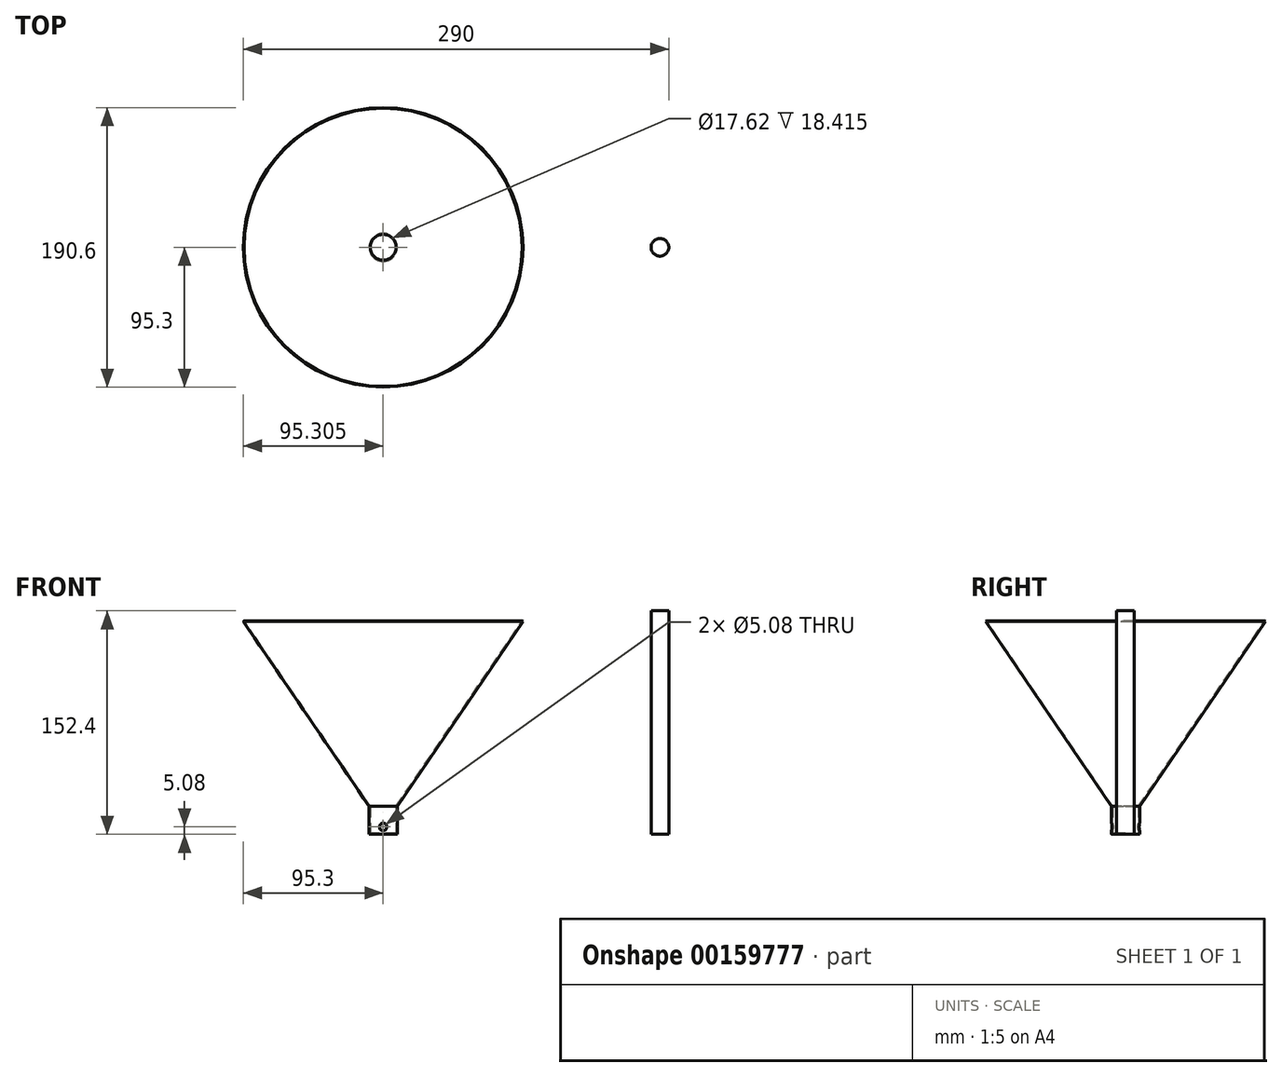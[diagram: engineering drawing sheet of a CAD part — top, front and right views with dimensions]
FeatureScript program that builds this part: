
annotation { "Feature Type Name" : "Feature", "Feature Type Description" : "" }
export const myFeature = defineFeature(function(context is Context, id is Id, definition is map)
    precondition{}
    {
        {
            var Q0;
            Q0=qCreatedBy(makeId("Top.planeOp"),FACE);
            var sketch = newSketch(context, id + "F0", { "sketchPlane" : qUnion([Q0])});
            skCircle(sketch, "E0", {"center": v(0, 0) * mm, "radius": 6.35 * mm});
            skSolve(sketch);
        }
        {
            var Q0;
            Q0=makeQuery(id+"F0.imprint","IMPRINT",FACE,{"disambiguationData":[TD([[makeQuery(id+"F0.imprint","IMPRINT",EDGE,{"derivedFrom":sQuery(id+"F0.wireOp",EDGE,"E0")}),1.0]])]});
            extrude(context, id + "F1", {"entities" : qUnion([Q0]), "depth" : 0.64 * mm});
        }
        {
            var Q0;
            Q0=makeQuery(id+"F1.opExtrude","CAP_FACE",FACE,{"disambiguationData":[OSD([sQuery(id+"F0.wireOp",EDGE,"E0")])],"isStart":false});
            var sketch = newSketch(context, id + "F2", { "sketchPlane" : qUnion([Q0])});
            skCircle(sketch, "E1", {"center": v(0, 0) * mm, "radius": 5.72 * mm});
            skSolve(sketch);
        }
        {
            var Q0;
            Q0=makeQuery(id+"F2.imprint","IMPRINT",FACE,{"disambiguationData":[TD([[makeQuery(id+"F2.imprint","IMPRINT",EDGE,{"derivedFrom":sQuery(id+"F2.wireOp",EDGE,"E1")}),-1.0]])]});
            extrude(context, id + "F3", {"entities" : qUnion([Q0]), "operationType" : NewBodyOperationType.ADD, "depth" : 12.7 * mm});
        }
        {
            var Q0;
            Q0=qCreatedBy(makeId("Front.planeOp"),FACE);
            var sketch = newSketch(context, id + "F4", { "sketchPlane" : qUnion([Q0])});
            skCircle(sketch, "E2", {"center": v(0, 3.18) * mm, "radius": 2.22 * mm});
            skSolve(sketch);
        }
        {
            var Q0;
            Q0=makeQuery(id+"F4.imprint","IMPRINT",FACE,{"disambiguationData":[TD([[makeQuery(id+"F4.imprint","IMPRINT",EDGE,{"derivedFrom":sQuery(id+"F4.wireOp",EDGE,"E2")}),1.0]])]});
            var Q1;
            Q1=sQuery(id+"F4.wireOp",EDGE,"E2");
            extrude(context, id + "F5", {"entities" : qUnion([Q0]), "operationType" : NewBodyOperationType.REMOVE, "surfaceEntities" : qUnion([Q1]), "endBound" : BoundingType.THROUGH_ALL, "oppositeDirection" : true, "depth" : 25.4 * mm, "hasSecondDirection" : true, "secondDirectionBound" : SecondDirectionBoundingType.THROUGH_ALL, "secondDirectionOppositeDirection" : false, "secondDirectionDepth" : 25.4 * mm});
        }
        {
            var Q0;
            Q0=qCreatedBy(makeId("Top.planeOp"),FACE);
            var sketch = newSketch(context, id + "F6", { "sketchPlane" : qUnion([Q0])});
            skCircle(sketch, "E3", {"center": v(34.06, 0) * mm, "radius": 6.03 * mm});
            skSolve(sketch);
        }
        {
            var Q0;
            Q0=makeQuery(id+"F6.imprint","IMPRINT",FACE,{"disambiguationData":[TD([[makeQuery(id+"F6.imprint","IMPRINT",EDGE,{"derivedFrom":sQuery(id+"F6.wireOp",EDGE,"E3")}),1.0]])]});
            extrude(context, id + "F7", {"entities" : qUnion([Q0]), "depth" : 152.4 * mm});
        }
        {
            var Q0;
            Q0=qCreatedBy(makeId("Front.planeOp"),FACE);
            var sketch = newSketch(context, id + "F8", { "sketchPlane" : qUnion([Q0])});
            skLineSegment(sketch, "E4", {"start": v(-145.8, 0) * mm, "end": v(-145.8, 19.05) * mm});
            skLineSegment(sketch, "E5", {"start": v(-145.8, 19.05) * mm, "end": v(-59.83, 145.41) * mm});
            skLineSegment(sketch, "E6", {"start": v(-59.83, 145.41) * mm, "end": v(-59.3, 145.05) * mm});
            skLineSegment(sketch, "E7", {"start": v(-59.3, 145.05) * mm, "end": v(-145.02, 19.05) * mm});
            skLineSegment(sketch, "E8", {"start": v(-145.02, 19.05) * mm, "end": v(-145.02, 0) * mm});
            skLineSegment(sketch, "E9", {"start": v(-145.02, 0) * mm, "end": v(-145.8, 0) * mm});
            skSolve(sketch);
        }
        {
            var Q0;
            Q0=qCreatedBy(makeId("Top.planeOp"),FACE);
            var sketch = newSketch(context, id + "F9", { "sketchPlane" : qUnion([Q0])});
            skCircle(sketch, "E10", {"center": v(-154.6, 0) * mm, "radius": 9.58 * mm});
            skSolve(sketch);
        }
        {
            var Q0;
            Q0=makeQuery(id+"F8.imprint","IMPRINT",FACE,{"disambiguationData":[TD([[makeQuery(id+"F8.imprint","IMPRINT",EDGE,{"derivedFrom":sQuery(id+"F8.wireOp",EDGE,"E4")}),-1.0]])]});
            var Q1;
            Q1=sQuery(id+"F9.wireOp",EDGE,"E10");
            revolve(context, id + "F10", {"entities" : qUnion([Q0]), "axis" : qUnion([Q1]), "revolveType" : RevolveType.FULL});
        }
        {
            var Q0;
            Q0=makeQuery(id+"F1.opExtrude","SWEPT_BODY",BODY,{"disambiguationData":[OSD([sQuery(id+"F0.wireOp",EDGE,"E0")])]});
            deleteBodies(context, id + "F11", {"entities" : qUnion([Q0])});
        }
        {
            var Q0;
            Q0=qCreatedBy(makeId("Front.planeOp"),FACE);
            var sketch = newSketch(context, id + "F12", { "sketchPlane" : qUnion([Q0])});
            skCircle(sketch, "E11", {"center": v(-154.6, 5.08) * mm, "radius": 2.54 * mm});
            skSolve(sketch);
        }
        {
            var Q0;
            Q0 = qSketchRegion(id + "F12", true);
            extrude(context, id + "F13", {"entities" : qUnion([Q0]), "operationType" : NewBodyOperationType.REMOVE, "endBound" : BoundingType.THROUGH_ALL, "oppositeDirection" : true, "depth" : 25.4 * mm, "hasSecondDirection" : true, "secondDirectionBound" : SecondDirectionBoundingType.THROUGH_ALL, "secondDirectionOppositeDirection" : false, "secondDirectionDepth" : 25.4 * mm});
        }
        {
            var Q0;
            Q0 = qSketchRegion(id + "F9", true);
            extrude(context, id + "F14", {"entities" : qUnion([Q0]), "operationType" : NewBodyOperationType.ADD, "depth" : 0.64 * mm});
        }
    });
